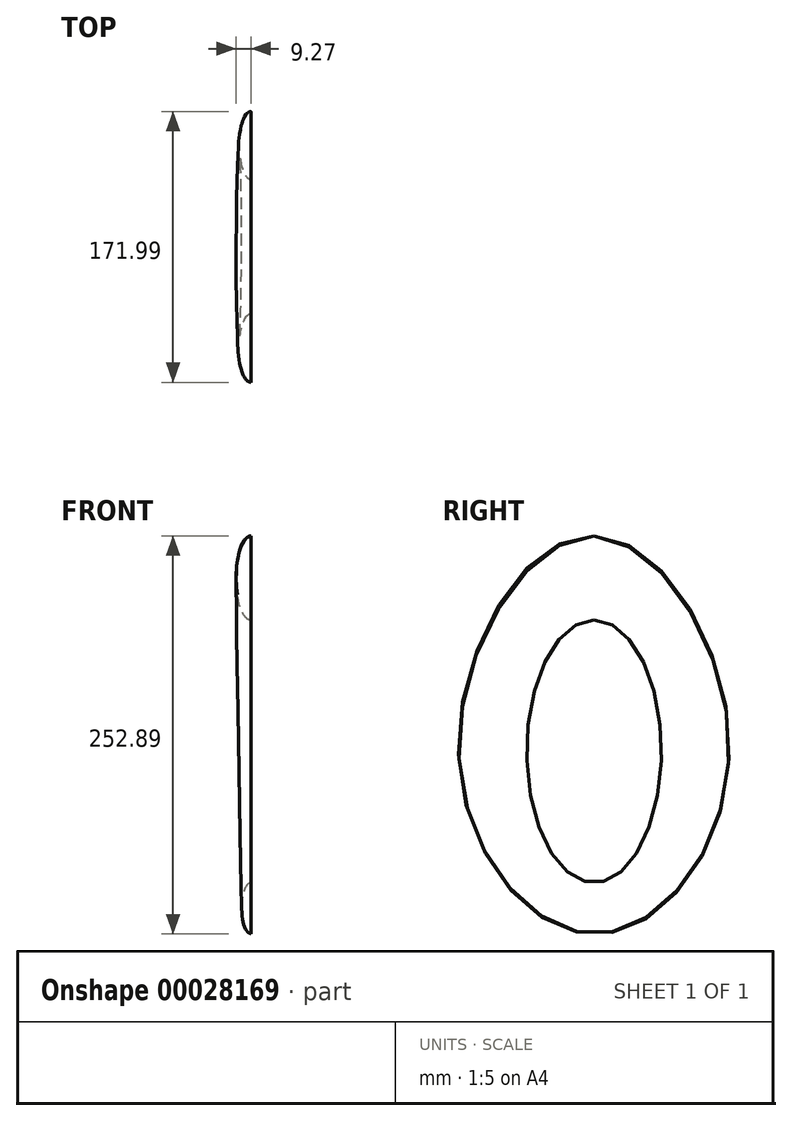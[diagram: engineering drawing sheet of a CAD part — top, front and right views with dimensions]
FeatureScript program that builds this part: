
annotation { "Feature Type Name" : "Feature", "Feature Type Description" : "" }
export const myFeature = defineFeature(function(context is Context, id is Id, definition is map)
    precondition{}
    {
        {
            var Q0;
            Q0=qCreatedBy(makeId("Right.planeOp"),FACE);
            var sketch = newSketch(context, id + "F0", { "sketchPlane" : qUnion([Q0])});
            skEllipse(sketch, "E0", {"center": v(0, 0) * mm, "majorRadius": 83.37 * mm, "minorRadius": 42.8 * mm, "majorAxis": v(0, 1)});
            skSolve(sketch);
        }
        {
            var Q0;
            Q0=makeQuery(id+"F0.imprint","IMPRINT",FACE,{"disambiguationData":[TD([[makeQuery(id+"F0.imprint","IMPRINT",EDGE,{"derivedFrom":sQuery(id+"F0.wireOp",EDGE,"E0")}),1.0]])]});
            var sketch = newSketch(context, id + "F1", { "sketchPlane" : qUnion([Q0])});
            skEllipticalArc(sketch, "E1", {});
            skEllipticalArc(sketch, "E2", {});
            const initialGuessF1  = {"E1": [0, 0, 0, 1, 0.08337347954511642, 0.04279728615157911, 0.8357064214483635, 4.029619640728345], "E2": [0, 0, 0, 1, 0.08337347954511642, 0.04279728615157911, 4.029619640728345, 0.8357064214483635]};
            skSetInitialGuess(sketch, initialGuessF1);
            skSolve(sketch);
        }
        {
            var Q0;
            Q0=qCreatedBy(makeId("Front.planeOp"),FACE);
            var sketch = newSketch(context, id + "F2", { "sketchPlane" : qUnion([Q0])});
            skEllipticalArc(sketch, "E3", {});
            skPoint(sketch, "E4", {"position": v(0, 83.37) * mm});
            skPoint(sketch, "E5", {"position": v(0, -83.37) * mm});
            skEllipticalArc(sketch, "E6", {});
            skLineSegment(sketch, "E7", {"start": v(0, 83.37) * mm, "end": v(0, 136.88) * mm});
            skLineSegment(sketch, "E8", {"start": v(0, -115.95) * mm, "end": v(0, -83.37) * mm});
            const initialGuessF2  = {"E3": [0, -0.09966069459915161, 0, -1, 0.016287215054035187, 0.005870050957731566, 3.141592653589793, 0], "E6": [0, 0.11012912541627884, 0, -1, 0.026755645871162415, 0.009261991864517304, 3.141592653589793, 0]};
            skSetInitialGuess(sketch, initialGuessF2);
            skSolve(sketch);
        }
        {
            var Q0;
            Q0=sQuery(id+"F2.wireOp",EDGE,"E6");
            var Q1;
            Q1=sQuery(id+"F2.wireOp",EDGE,"E3");
            var Q2;
            Q2 = qConstructionFilter(qBodyType(qCreatedBy(id + "F1" ,EDGE), BodyType.WIRE), ConstructionObject.NO);
            loft(context, id + "F3", {"bodyType" : ToolBodyType.SURFACE, "addGuides" : true, "wireProfilesArray" : [{ "wireProfileEntities" : qUnion([Q0]) }, { "wireProfileEntities" : qUnion([Q1]) }], "guidesArray" : [{ "guideEntities" : qUnion([Q2]), "guideDerivativeType" : LoftGuideDerivativeType.DEFAULT, "guideDerivativeMagnitude" : 1 }]});
        }
        {
            var Q0;
            Q0=sQuery(id+"F2.wireOp",EDGE,"E7");
            var Q1;
            Q1=sQuery(id+"F2.wireOp",EDGE,"E8");
            var Q2;
            Q2=sQuery(id+"F0.wireOp",EDGE,"E0");
            loft(context, id + "F4", {"bodyType" : ToolBodyType.SURFACE, "addGuides" : true, "wireProfilesArray" : [{ "wireProfileEntities" : qUnion([Q0]) }, { "wireProfileEntities" : qUnion([Q1]) }], "guidesArray" : [{ "guideEntities" : qUnion([Q2]), "guideDerivativeType" : LoftGuideDerivativeType.DEFAULT, "guideDerivativeMagnitude" : 1 }]});
        }
    });
